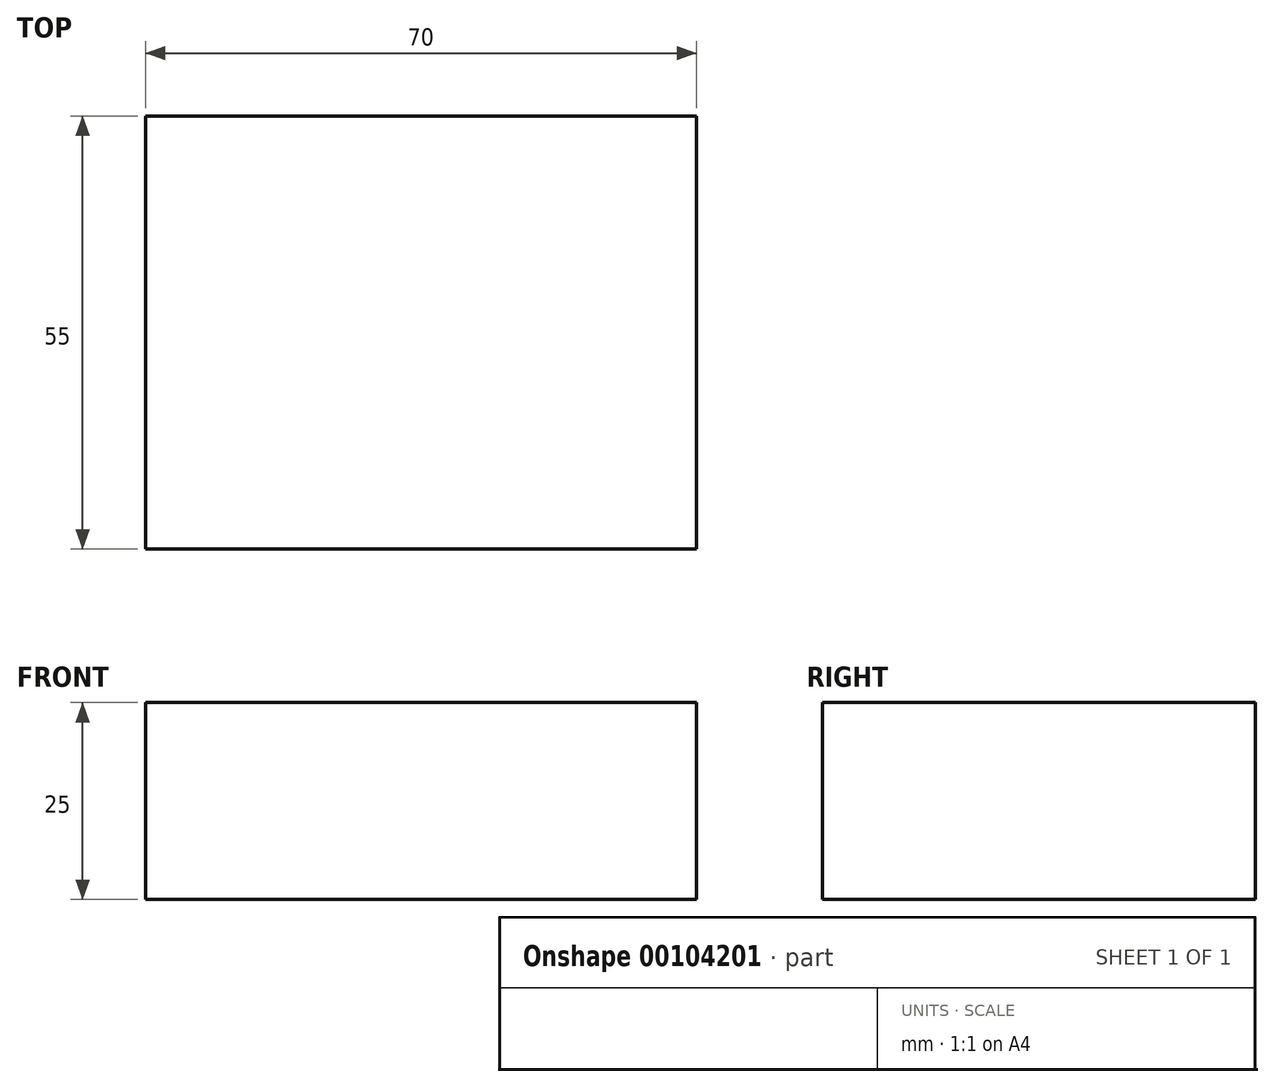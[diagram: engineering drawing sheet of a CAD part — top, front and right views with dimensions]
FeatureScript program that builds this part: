
annotation { "Feature Type Name" : "Feature", "Feature Type Description" : "" }
export const myFeature = defineFeature(function(context is Context, id is Id, definition is map)
    precondition{}
    {
        {
            var Q0;
            Q0=qCreatedBy(makeId("Top.planeOp"),FACE);
            var sketch = newSketch(context, id + "F0", { "sketchPlane" : qUnion([Q0])});
            skLineSegment(sketch, "E0.bottom", {"start": v(-38.66, 28.88) * mm, "end": v(31.34, 28.88) * mm});
            skLineSegment(sketch, "E0.top", {"start": v(-38.66, -26.12) * mm, "end": v(31.34, -26.12) * mm});
            skLineSegment(sketch, "E0.left", {"start": v(-38.66, 28.88) * mm, "end": v(-38.66, -26.12) * mm});
            skLineSegment(sketch, "E0.right", {"start": v(31.34, 28.88) * mm, "end": v(31.34, -26.12) * mm});
            skSolve(sketch);
        }
        {
            var Q0;
            Q0=makeQuery(id+"F0.imprint","IMPRINT",FACE,{"disambiguationData":[TD([[makeQuery(id+"F0.imprint","IMPRINT",EDGE,{"derivedFrom":sQuery(id+"F0.wireOp",EDGE,"E0.bottom")}),-1.0]])]});
            extrude(context, id + "F1", {"entities" : qUnion([Q0]), "depth" : 25 * mm});
        }
    });
